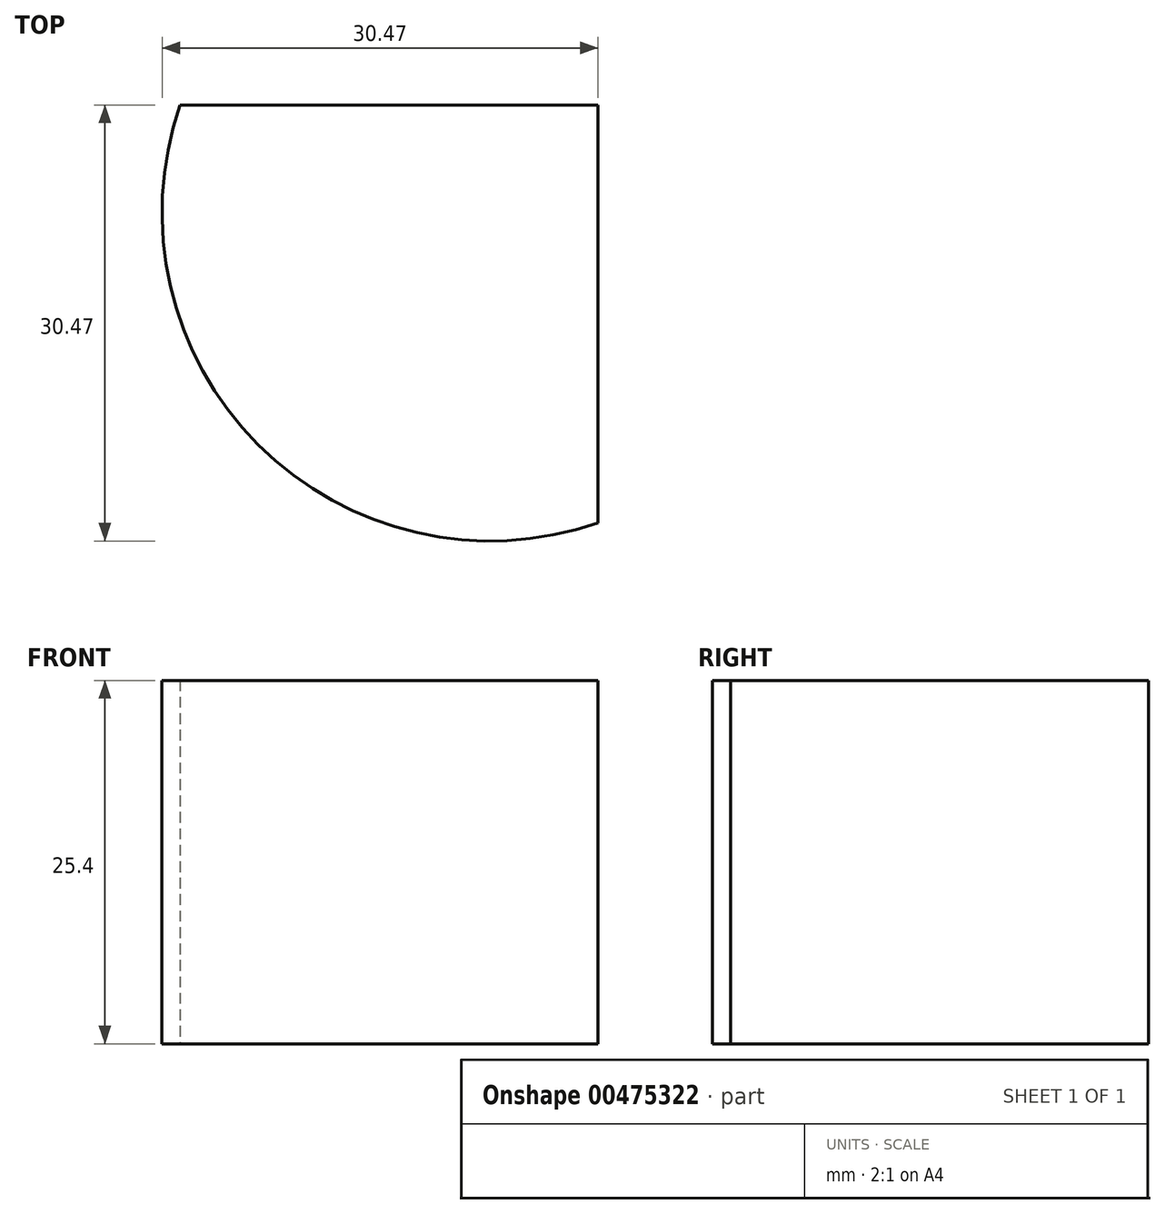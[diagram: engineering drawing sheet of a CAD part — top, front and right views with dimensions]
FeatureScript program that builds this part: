
annotation { "Feature Type Name" : "Feature", "Feature Type Description" : "" }
export const myFeature = defineFeature(function(context is Context, id is Id, definition is map)
    precondition{}
    {
        {
            var Q0;
            Q0=qCreatedBy(makeId("Top.planeOp"),FACE);
            var sketch = newSketch(context, id + "F0", { "sketchPlane" : qUnion([Q0])});
            skLineSegment(sketch, "E0", {"start": v(0, 0) * mm, "end": v(-29.21, 0) * mm});
            skLineSegment(sketch, "E1", {"start": v(0, 0) * mm, "end": v(0, -29.21) * mm});
            skArc(sketch, "E2", {"start": v(-29.21, 0) * mm, "mid": v(-23.75, -23.75) * mm, "end": v(0, -29.2) * mm});
            skSolve(sketch);
        }
        {
            var Q0;
            Q0=makeQuery(id+"F0.imprint","IMPRINT",FACE,{"disambiguationData":[TD([[makeQuery(id+"F0.imprint","IMPRINT",EDGE,{"derivedFrom":sQuery(id+"F0.wireOp",EDGE,"E0")}),1.0]])]});
            var Q1;
            Q1=sQuery(id+"F0.wireOp",EDGE,"E2");
            extrude(context, id + "F1", {"entities" : qUnion([Q0]), "surfaceEntities" : qUnion([Q1]), "depth" : 25.4 * mm});
        }
    });
